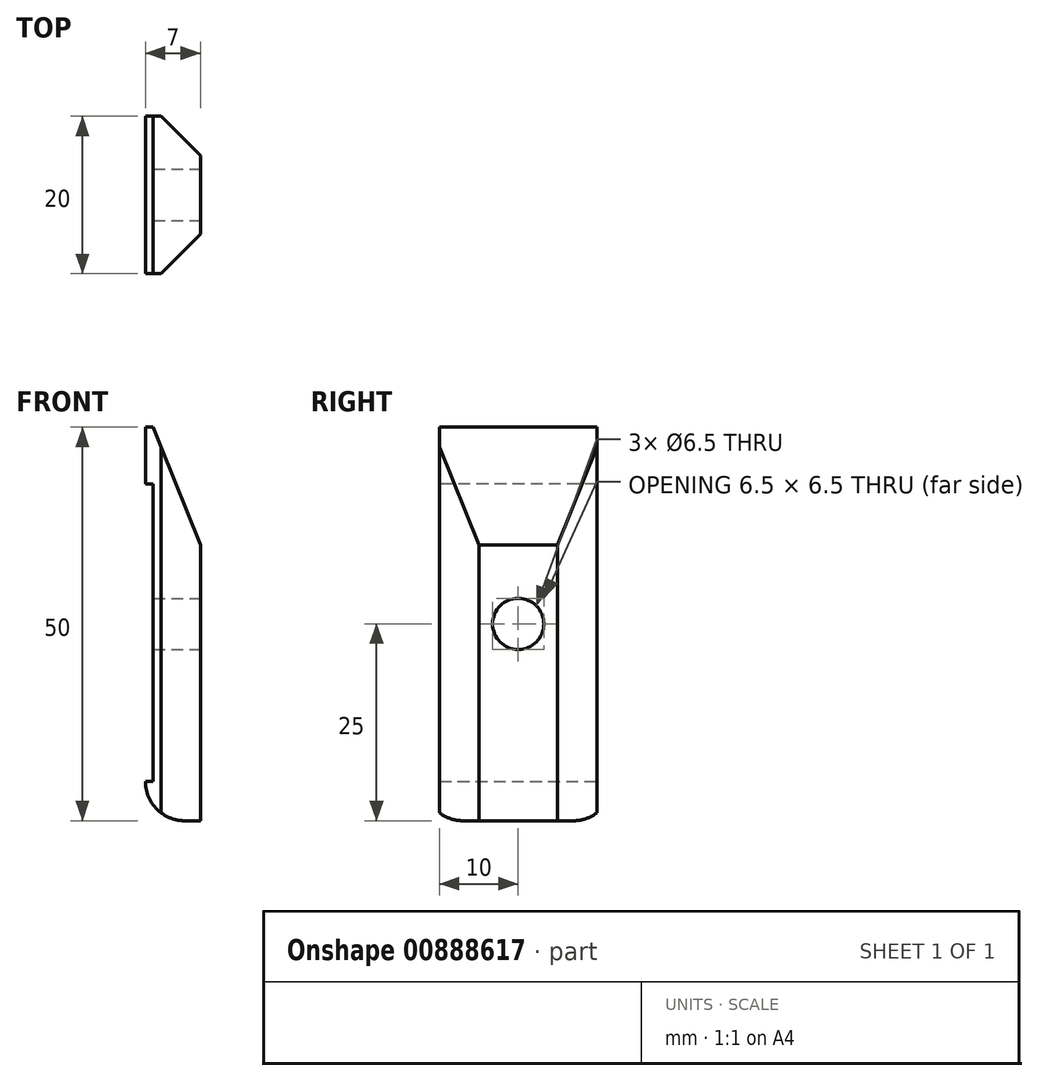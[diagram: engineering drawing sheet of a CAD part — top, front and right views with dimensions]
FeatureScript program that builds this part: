
annotation { "Feature Type Name" : "Feature", "Feature Type Description" : "" }
export const myFeature = defineFeature(function(context is Context, id is Id, definition is map)
    precondition{}
    {
        {
            var Q0;
            Q0=qCreatedBy(makeId("Front.planeOp"),FACE);
            var sketch = newSketch(context, id + "F0", { "sketchPlane" : qUnion([Q0])});
            skLineSegment(sketch, "E0.bottom", {"start": v(3.5, 25) * mm, "end": v(-3.5, 25) * mm});
            skLineSegment(sketch, "E0.top", {"start": v(3.5, -25) * mm, "end": v(-3.5, -25) * mm});
            skLineSegment(sketch, "E0.left", {"start": v(3.5, 25) * mm, "end": v(3.5, -25) * mm});
            skLineSegment(sketch, "E0.right", {"start": v(-3.5, 25) * mm, "end": v(-3.5, -25) * mm});
            skPoint(sketch, "E0.middle", {"position": v(0, 0) * mm});
            skSolve(sketch);
        }
        {
            var Q0;
            Q0=makeQuery(id+"F0.imprint","IMPRINT",FACE,{"disambiguationData":[TD([[makeQuery(id+"F0.imprint","IMPRINT",EDGE,{"derivedFrom":sQuery(id+"F0.wireOp",EDGE,"E0.bottom")}),1.0]])]});
            extrude(context, id + "F1", {"entities" : qUnion([Q0]), "depth" : 20 * mm, "offsetDistance" : 25 * mm});
        }
        {
            var Q0;
            Q0=makeQuery(id+"F1.opExtrude","SWEPT_EDGE",EDGE,{"disambiguationData":[OSD([sQuery(id+"F0.wireOp",EDGE,"E0.top"),sQuery(id+"F0.wireOp",EDGE,"E0.right")])]});
            fillet(context, id + "F2", {"entities" : qUnion([Q0]), "radius" : 5 * mm, "tangentPropagation" : true, "allowEdgeOverflow" : false});
        }
        {
            var Q0;
            Q0=makeQuery(id+"F1.opExtrude","SWEPT_FACE",FACE,{"disambiguationData":[OSD([sQuery(id+"F0.wireOp",EDGE,"E0.right")])]});
            var sketch = newSketch(context, id + "F3", { "sketchPlane" : qUnion([Q0])});
            skLineSegment(sketch, "E1.bottom", {"start": v(0, -20) * mm, "end": v(20, -20) * mm});
            skLineSegment(sketch, "E1.top", {"start": v(0, 17.75) * mm, "end": v(20, 17.75) * mm});
            skLineSegment(sketch, "E1.left", {"start": v(0, -20) * mm, "end": v(0, 17.75) * mm});
            skLineSegment(sketch, "E1.right", {"start": v(20, -20) * mm, "end": v(20, 17.75) * mm});
            skSolve(sketch);
        }
        {
            var Q0;
            Q0=makeQuery(id+"F3.imprint","IMPRINT",FACE,{"disambiguationData":[TD([[makeQuery(id+"F3.imprint","IMPRINT",EDGE,{"derivedFrom":sQuery(id+"F3.wireOp",EDGE,"E1.bottom")}),1.0]])]});
            extrude(context, id + "F4", {"entities" : qUnion([Q0]), "operationType" : NewBodyOperationType.REMOVE, "oppositeDirection" : true, "depth" : 1 * mm, "offsetDistance" : 25 * mm});
        }
        {
            var Q0;
            Q0=makeQuery(id+"F1.opExtrude","SWEPT_EDGE",EDGE,{"disambiguationData":[OSD([sQuery(id+"F0.wireOp",EDGE,"E0.bottom"),sQuery(id+"F0.wireOp",EDGE,"E0.left")])]});
            chamfer(context, id + "F5", {"entities" : qUnion([Q0]), "chamferType" : ChamferType.TWO_OFFSETS, "width1" : 6 * mm, "oppositeDirection" : false, "width2" : 15 * mm, "tangentPropagation" : true});
        }
        {
            var Q0;
            Q0=makeQuery(id+"F1.opExtrude","SWEPT_FACE",FACE,{"disambiguationData":[OSD([sQuery(id+"F0.wireOp",EDGE,"E0.left")])]});
            var sketch = newSketch(context, id + "F6", { "sketchPlane" : qUnion([Q0])});
            skCircle(sketch, "E2", {"center": v(-10, 0) * mm, "radius": 3.25 * mm});
            skPoint(sketch, "E2.centerSnap0", {"position": v(-10, -25) * mm});
            skSolve(sketch);
        }
        {
            var Q0;
            Q0=makeQuery(id+"F6.imprint","IMPRINT",FACE,{"disambiguationData":[TD([[makeQuery(id+"F6.imprint","IMPRINT",EDGE,{"derivedFrom":sQuery(id+"F6.wireOp",EDGE,"E2")}),1.0]])]});
            extrude(context, id + "F7", {"entities" : qUnion([Q0]), "operationType" : NewBodyOperationType.REMOVE, "oppositeDirection" : true, "depth" : 25 * mm, "offsetDistance" : 25 * mm});
        }
        {
            var Q0;
            Q0=makeQuery(id+"F1.opExtrude","CAP_EDGE",EDGE,{"disambiguationData":[OSD([sQuery(id+"F0.wireOp",EDGE,"E0.left")])],"isStart":false});
            var Q1;
            Q1=makeQuery(id+"F1.opExtrude","CAP_EDGE",EDGE,{"disambiguationData":[OSD([sQuery(id+"F0.wireOp",EDGE,"E0.left")])],"isStart":true});
            chamfer(context, id + "F8", {"entities" : qUnion([Q0, Q1]), "width" : 5 * mm, "tangentPropagation" : true});
        }
    });
